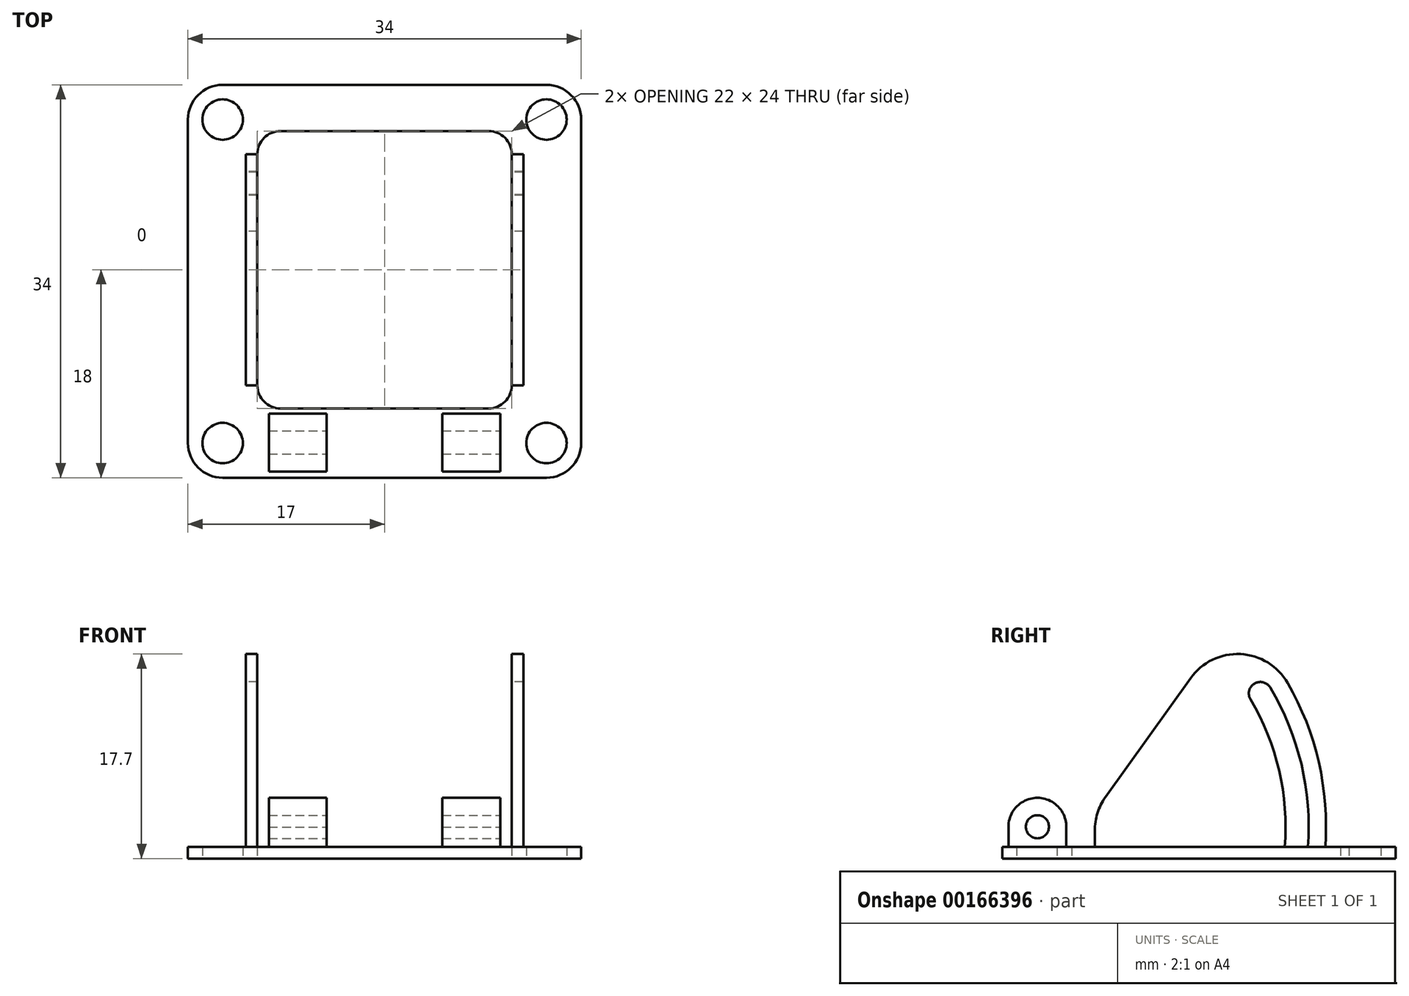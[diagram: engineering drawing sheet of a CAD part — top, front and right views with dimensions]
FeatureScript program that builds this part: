
annotation { "Feature Type Name" : "Feature", "Feature Type Description" : "" }
export const myFeature = defineFeature(function(context is Context, id is Id, definition is map)
    precondition{}
    {
        {
            var Q0;
            Q0=qCreatedBy(makeId("Top.planeOp"),FACE);
            var sketch = newSketch(context, id + "F0", { "sketchPlane" : qUnion([Q0])});
            skCircle(sketch, "E0", {"center": v(-14, 14) * mm, "radius": 1.75 * mm});
            skCircle(sketch, "E1", {"center": v(14, 14) * mm, "radius": 1.75 * mm});
            skCircle(sketch, "E2", {"center": v(14, -14) * mm, "radius": 1.75 * mm});
            skCircle(sketch, "E3", {"center": v(-14, -14) * mm, "radius": 1.75 * mm});
            skArc(sketch, "E4", {"start": v(-14, 17) * mm, "mid": v(-16.12, 16.12) * mm, "end": v(-17, 14) * mm});
            skArc(sketch, "E5", {"start": v(17, 14) * mm, "mid": v(16.12, 16.12) * mm, "end": v(14, 17) * mm});
            skArc(sketch, "E6", {"start": v(14, -17) * mm, "mid": v(16.12, -16.12) * mm, "end": v(17, -14) * mm});
            skArc(sketch, "E7", {"start": v(-17, -14) * mm, "mid": v(-16.12, -16.12) * mm, "end": v(-14, -17) * mm});
            skLineSegment(sketch, "E8", {"start": v(-17, 14) * mm, "end": v(-17, -14) * mm});
            skLineSegment(sketch, "E9", {"start": v(-14, -17) * mm, "end": v(14, -17) * mm});
            skLineSegment(sketch, "E10", {"start": v(17, -14) * mm, "end": v(17, 14) * mm});
            skLineSegment(sketch, "E11", {"start": v(14, 17) * mm, "end": v(-14, 17) * mm});
            skLineSegment(sketch, "E12", {"start": v(0, 17) * mm, "end": v(0, -17) * mm});
            skLineSegment(sketch, "E13.0", {"start": v(-11, 11) * mm, "end": v(-11, -9) * mm});
            skLineSegment(sketch, "E14.0", {"start": v(11, 11) * mm, "end": v(11, -9) * mm});
            skLineSegment(sketch, "E15.0", {"start": v(9, 13) * mm, "end": v(-9, 13) * mm});
            skLineSegment(sketch, "E16.0", {"start": v(-9, -11) * mm, "end": v(9, -11) * mm});
            skArc(sketch, "E17.filletArc", {"start": v(-9, 13) * mm, "mid": v(-10.41, 12.41) * mm, "end": v(-11, 11) * mm});
            skArc(sketch, "E18.filletArc", {"start": v(-11, -9) * mm, "mid": v(-10.41, -10.41) * mm, "end": v(-9, -11) * mm});
            skArc(sketch, "E19.filletArc", {"start": v(9, -11) * mm, "mid": v(10.41, -10.41) * mm, "end": v(11, -9) * mm});
            skArc(sketch, "E20.filletArc", {"start": v(11, 11) * mm, "mid": v(10.41, 12.41) * mm, "end": v(9, 13) * mm});
            skSolve(sketch);
        }
        {
            var Q0;
            Q0 = qSketchRegion(id + "F0", true);
            extrude(context, id + "F1", {"entities" : qUnion([Q0]), "depth" : 1 * mm});
        }
        {
            var Q0;
            Q0=makeQuery(id+"F1.opExtrude","SWEPT_FACE",FACE,{"disambiguationData":[OSD([sQuery(id+"F0.wireOp",EDGE,"E14.0")])]});
            var sketch = newSketch(context, id + "F2", { "sketchPlane" : qUnion([Q0])});
            skLineSegment(sketch, "E21", {"start": v(9, 2.4) * mm, "end": v(9, 1) * mm});
            skLineSegment(sketch, "E22", {"start": v(9, 1) * mm, "end": v(14, 1) * mm});
            skLineSegment(sketch, "E23.0", {"start": v(8.07, 5.3) * mm, "end": v(0.72, 15.6) * mm});
            skPoint(sketch, "E24.newPointA", {"position": v(14, 1) * mm});
            skArc(sketch, "E25.filletArc", {"start": v(9, 2.4) * mm, "mid": v(8.76, 3.93) * mm, "end": v(8.07, 5.3) * mm});
            skLineSegment(sketch, "E26", {"start": v(14, 1) * mm, "end": v(14, 2.75) * mm});
            skArc(sketch, "E27", {"start": v(-6.18, 14.79) * mm, "mid": v(-8.87, 8.14) * mm, "end": v(-9.43, 1) * mm});
            skArc(sketch, "E28", {"start": v(-4.47, 13.76) * mm, "mid": v(-6.94, 7.61) * mm, "end": v(-7.43, 1) * mm});
            skArc(sketch, "E29", {"start": v(-7.69, 15.18) * mm, "mid": v(-10.37, 8.33) * mm, "end": v(-10.94, 1) * mm});
            skLineSegment(sketch, "E30.0", {"start": v(-14, 1) * mm, "end": v(14, 1) * mm});
            skPoint(sketch, "E31.visualSharp", {"position": v(-3.12, 20.97) * mm});
            skArc(sketch, "E31.filletArc", {"start": v(0.72, 15.6) * mm, "mid": v(-3.6, 17.69) * mm, "end": v(-7.69, 15.18) * mm});
            skArc(sketch, "E32", {"start": v(-4.47, 13.76) * mm, "mid": v(-4.81, 15.13) * mm, "end": v(-6.18, 14.79) * mm});
            skSolve(sketch);
        }
        {
            var Q0;
            {var subQ2=sQuery(id+"F2.wireOp",EDGE,"E21");Q0=makeQuery(id+"F2.imprint","IMPRINT",FACE,{"disambiguationData":[TD([[makeQuery(id+"F2.imprint","IMPRINT",EDGE,{"derivedFrom":subQ2}),-1.0]])]});}
            extrude(context, id + "F3", {"entities" : qUnion([Q0]), "oppositeDirection" : true, "depth" : 1 * mm});
        }
        {
            var Q0;
            Q0=makeQuery(id+"F3.opExtrude","SWEPT_BODY",BODY,{"disambiguationData":[OSD([sQuery(id+"F0.wireOp",EDGE,"E14.0"),sQuery(id+"F2.wireOp",EDGE,"E21"),sQuery(id+"F2.wireOp",EDGE,"Wprl2ymM-YVw9-F5b7-PARr-VH9FuCP09HX2"),sQuery(id+"F2.wireOp",EDGE,"IV3tOoaO-t3fY-cnzm-duXL-VoCPUKAFI89S"),sQuery(id+"F2.wireOp",EDGE,"MGhXAGIA-fIAS-gHYs-iBJj-tU0ugR5plCXY"),sQuery(id+"F2.wireOp",EDGE,"41fa4243-c2a2-416b-abb1-f1db0d147dff.0"),sQuery(id+"F2.wireOp",EDGE,"E23.0"),sQuery(id+"F2.wireOp",EDGE,"b9e57630-953d-4844-99b6-cea640d2f4c5.filletArc"),sQuery(id+"F2.wireOp",EDGE,"E25.filletArc")])]});
            transform(context, id + "F4", {"entities" : qUnion([Q0]), "transformType" : TransformType.TRANSLATION_3D, "dx" : -23 * mm, "dy" : 0 * mm, "dz" : 0 * mm, "makeCopy" : true});
        }
        {
            var Q0;
            Q0=qCreatedBy(makeId("Right.planeOp"),FACE);
            var sketch = newSketch(context, id + "F5", { "sketchPlane" : qUnion([Q0])});
            skCircle(sketch, "E33", {"center": v(-13.95, 2.75) * mm, "radius": 1 * mm});
            skArc(sketch, "E34", {"start": v(-11.45, 2.7) * mm, "mid": v(-13.93, 5.25) * mm, "end": v(-16.45, 2.75) * mm});
            skLineSegment(sketch, "E35", {"start": v(-11.45, 2.8) * mm, "end": v(-11.45, 1.01) * mm});
            skLineSegment(sketch, "E36", {"start": v(-16.45, 2.75) * mm, "end": v(-16.45, 0.98) * mm});
            skLineSegment(sketch, "E37", {"start": v(-16.45, 0.98) * mm, "end": v(-11.45, 1.01) * mm});
            skSolve(sketch);
        }
        {
            var Q0;
            Q0 = qSketchRegion(id + "F5", true);
            extrude(context, id + "F6", {"entities" : qUnion([Q0]), "oppositeDirection" : true, "depth" : 5 * mm});
        }
        {
            var Q0;
            Q0=makeQuery(id+"F6.opExtrude","SWEPT_BODY",BODY,{"disambiguationData":[OSD([sQuery(id+"F5.wireOp",EDGE,"E33"),sQuery(id+"F5.wireOp",EDGE,"E34"),sQuery(id+"F5.wireOp",EDGE,"E35"),sQuery(id+"F5.wireOp",EDGE,"E36"),sQuery(id+"F5.wireOp",EDGE,"E37")])]});
            transform(context, id + "F7", {"entities" : qUnion([Q0]), "transformType" : TransformType.TRANSLATION_3D, "dx" : -5 * mm, "dy" : 0 * mm, "dz" : 0 * mm, "makeCopy" : false});
        }
        {
            var Q0;
            Q0=makeQuery(id+"F6.opExtrude","SWEPT_BODY",BODY,{"disambiguationData":[OSD([sQuery(id+"F5.wireOp",EDGE,"E33"),sQuery(id+"F5.wireOp",EDGE,"E34"),sQuery(id+"F5.wireOp",EDGE,"E35"),sQuery(id+"F5.wireOp",EDGE,"E36"),sQuery(id+"F5.wireOp",EDGE,"E37")])]});
            transform(context, id + "F8", {"entities" : qUnion([Q0]), "transformType" : TransformType.TRANSLATION_3D, "dx" : 15 * mm, "dy" : 0 * mm, "dz" : 0 * mm, "makeCopy" : true});
        }
    });
